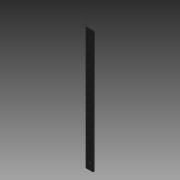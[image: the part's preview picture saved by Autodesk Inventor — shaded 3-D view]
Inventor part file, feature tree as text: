
AUTODESK INVENTOR PART (.ipt)
format: ipt  version: 2015 (Build 190159000, 159)  size: 156,160 bytes
history: native  units: mm
features: extrude x3, fillet x2, hole x1, other x1
ambient origin geometry x8: Origin, YZ Plane, XZ Plane, XY Plane, X Axis, Y Axis, Z Axis, Center Point
bodies: Solid1 (feature_tree)
feature tree (7):
  extrude  "Extrusión1"  Depth=1.5mm
  extrude  "Extrusión2"  Depth=15.0mm
  hole  "Agujero1"  [1 undecoded]
  fillet  "Empalme1"  [1 undecoded]
  extrude  "Extrusión3"  Depth=1.5mm
  fillet  "Redondeo de esquina1"  Radius=3.0mm
  other  "Definición1"
note: 2 required parameter values undecoded (feature->parameter linkage not recoverable at this tier; creation-order binding heuristic only, values carry confidence <= 0.55)
